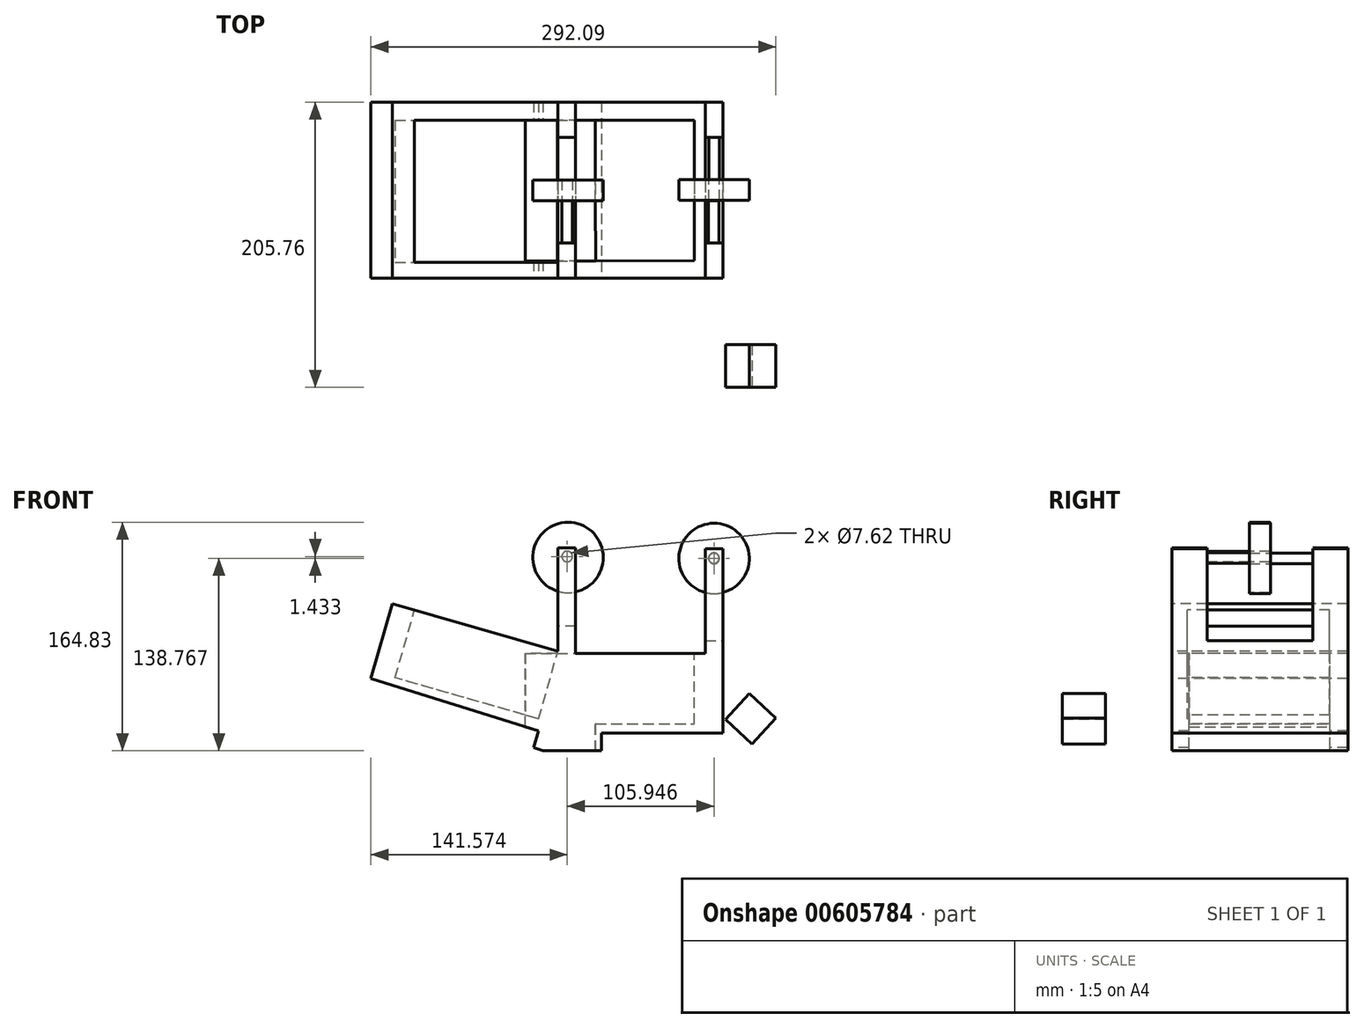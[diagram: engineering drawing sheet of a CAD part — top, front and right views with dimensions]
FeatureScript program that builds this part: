
annotation { "Feature Type Name" : "Feature", "Feature Type Description" : "" }
export const myFeature = defineFeature(function(context is Context, id is Id, definition is map)
    precondition{}
    {
        {
            var Q0;
            Q0=qCreatedBy(makeId("Front.planeOp"),FACE);
            var sketch = newSketch(context, id + "F0", { "sketchPlane" : qUnion([Q0])});
            skLineSegment(sketch, "E0", {"start": v(0, 0) * mm, "end": v(0, 57.54) * mm});
            skLineSegment(sketch, "E1", {"start": v(0, 57.54) * mm, "end": v(-113.43, 57.54) * mm});
            skLineSegment(sketch, "E2", {"start": v(-113.43, 57.54) * mm, "end": v(-238.5, 93.39) * mm});
            skLineSegment(sketch, "E3", {"start": v(-238.5, 93.39) * mm, "end": v(-254, 39.34) * mm});
            skLineSegment(sketch, "E4", {"start": v(-254, 39.34) * mm, "end": v(-127.98, 0) * mm});
            skLineSegment(sketch, "E5", {"start": v(-241.45, 83.14) * mm, "end": v(-250.88, 50.23) * mm});
            skLineSegment(sketch, "E6", {"start": v(-250.88, 50.23) * mm, "end": v(-287.5, 60.72) * mm});
            skLineSegment(sketch, "E7", {"start": v(-287.5, 60.72) * mm, "end": v(-241.45, 83.14) * mm});
            skLineSegment(sketch, "E8", {"start": v(0, 9.96) * mm, "end": v(0, 46.2) * mm});
            skLineSegment(sketch, "E9", {"start": v(0, 46.2) * mm, "end": v(38.1, 10.83) * mm});
            skLineSegment(sketch, "E10", {"start": v(38.1, 10.83) * mm, "end": v(0, 9.96) * mm});
            skLineSegment(sketch, "E11", {"start": v(-119.1, 59.16) * mm, "end": v(-119.1, 133.74) * mm});
            skLineSegment(sketch, "E12", {"start": v(-119.1, 133.74) * mm, "end": v(-106.4, 133.74) * mm});
            skLineSegment(sketch, "E13", {"start": v(-106.4, 133.74) * mm, "end": v(-106.4, 57.54) * mm});
            skLineSegment(sketch, "E14", {"start": v(-106.4, 57.54) * mm, "end": v(-113.43, 57.54) * mm});
            skLineSegment(sketch, "E15", {"start": v(0, 57.54) * mm, "end": v(0, 133.05) * mm});
            skLineSegment(sketch, "E16", {"start": v(0, 133.05) * mm, "end": v(-12.7, 133.05) * mm});
            skLineSegment(sketch, "E17", {"start": v(-12.7, 133.05) * mm, "end": v(-12.7, 57.54) * mm});
            skLineSegment(sketch, "E18", {"start": v(-12.7, 57.54) * mm, "end": v(0, 57.54) * mm});
            skLineSegment(sketch, "E19", {"start": v(-132.95, 1.55) * mm, "end": v(-136.74, -10.57) * mm});
            skLineSegment(sketch, "E20", {"start": v(-136.74, -10.57) * mm, "end": v(-129.91, -12.7) * mm});
            skLineSegment(sketch, "E21", {"start": v(-129.91, -12.7) * mm, "end": v(-87.6, -12.7) * mm});
            skLineSegment(sketch, "E22", {"start": v(-87.6, -12.7) * mm, "end": v(-87.6, 0) * mm});
            skLineSegment(sketch, "E23", {"start": v(-87.6, 0) * mm, "end": v(-127.98, 0) * mm});
            skLineSegment(sketch, "E24", {"start": v(19.05, 28.52) * mm, "end": v(43.47, 28.52) * mm});
            skLineSegment(sketch, "E25", {"start": v(43.47, 28.52) * mm, "end": v(43.47, 41.22) * mm});
            skLineSegment(sketch, "E26", {"start": v(43.47, 41.22) * mm, "end": v(5.37, 41.22) * mm});
            skLineSegment(sketch, "E27", {"start": v(5.37, 41.22) * mm, "end": v(19.05, 28.52) * mm});
            skLineSegment(sketch, "E28", {"start": v(0, 9.96) * mm, "end": v(0, 0) * mm});
            skLineSegment(sketch, "E29", {"start": v(-87.6, 0) * mm, "end": v(0, 0) * mm});
            skSolve(sketch);
        }
        {
            var Q0;
            Q0=makeQuery(id+"F0.imprint","IMPRINT",FACE,{"disambiguationData":[TD([[makeQuery(id+"F0.imprint","IMPRINT",EDGE,{"derivedFrom":sQuery(id+"F0.wireOp",EDGE,"E0")}),1.0]])]});
            var Q1;
            Q1=makeQuery(id+"F0.imprint","IMPRINT",FACE,{"disambiguationData":[TD([[makeQuery(id+"F0.imprint","IMPRINT",EDGE,{"derivedFrom":sQuery(id+"F0.wireOp",EDGE,"E5")}),-1.0]])]});
            var Q2;
            {var subQ0=sQuery(id+"F0.wireOp",EDGE,"E19");Q2=makeQuery(id+"F0.imprint","IMPRINT",FACE,{"disambiguationData":[TD([[makeQuery(id+"F0.imprint","IMPRINT",EDGE,{"derivedFrom":subQ0}),1.0]])]});}
            var Q3;
            {var subQ0=sQuery(id+"F0.wireOp",EDGE,"E11");Q3=makeQuery(id+"F0.imprint","IMPRINT",FACE,{"disambiguationData":[TD([[makeQuery(id+"F0.imprint","IMPRINT",EDGE,{"derivedFrom":subQ0}),-1.0]])]});}
            var Q4;
            Q4=makeQuery(id+"F0.imprint","IMPRINT",FACE,{"disambiguationData":[TD([[makeQuery(id+"F0.imprint","IMPRINT",EDGE,{"derivedFrom":sQuery(id+"F0.wireOp",EDGE,"E15")}),1.0]])]});
            var Q5;
            Q5=makeQuery(id+"F0.imprint","IMPRINT",FACE,{"disambiguationData":[TD([[makeQuery(id+"F0.imprint","IMPRINT",EDGE,{"derivedFrom":sQuery(id+"F0.wireOp",EDGE,"E24")}),1.0]])]});
            var Q6;
            {var subQ3=sQuery(id+"F0.wireOp",EDGE,"E8");Q6=makeQuery(id+"F0.imprint","IMPRINT",FACE,{"disambiguationData":[TD([[makeQuery(id+"F0.imprint","IMPRINT",EDGE,{"derivedFrom":subQ3}),-1.0]])]});}
            extrude(context, id + "F1", {"entities" : qUnion([Q0, Q1, Q2, Q3, Q4, Q5, Q6]), "oppositeDirection" : true, "depth" : 127 * mm, "offsetDistance" : 25.4 * mm});
        }
        {
            var Q0;
            Q0=makeQuery(id+"F1.opExtrude","SWEPT_FACE",FACE,{"disambiguationData":[OSD([sQuery(id+"F0.wireOp",EDGE,"E0"),sQuery(id+"F0.wireOp",EDGE,"E15")])]});
            var sketch = newSketch(context, id + "F2", { "sketchPlane" : qUnion([Q0])});
            skLineSegment(sketch, "E30", {"start": v(25.4, 133.05) * mm, "end": v(25.4, 66.79) * mm});
            skLineSegment(sketch, "E31", {"start": v(25.4, 66.79) * mm, "end": v(101.6, 66.79) * mm});
            skLineSegment(sketch, "E32", {"start": v(101.6, 66.79) * mm, "end": v(101.6, 133.05) * mm});
            skLineSegment(sketch, "E33", {"start": v(101.6, 133.05) * mm, "end": v(25.4, 133.05) * mm});
            skSolve(sketch);
        }
        {
            var Q0;
            Q0=makeQuery(id+"F2.imprint","IMPRINT",FACE,{"disambiguationData":[TD([[makeQuery(id+"F2.imprint","IMPRINT",EDGE,{"derivedFrom":sQuery(id+"F2.wireOp",EDGE,"E30")}),1.0]])]});
            extrude(context, id + "F3", {"entities" : qUnion([Q0]), "operationType" : NewBodyOperationType.REMOVE, "oppositeDirection" : true, "depth" : 25.4 * mm, "offsetDistance" : 25.4 * mm});
        }
        {
            var Q0;
            Q0=makeQuery(id+"F1.opExtrude","SWEPT_FACE",FACE,{"disambiguationData":[OSD([sQuery(id+"F0.wireOp",EDGE,"E11")])]});
            var sketch = newSketch(context, id + "F4", { "sketchPlane" : qUnion([Q0])});
            skLineSegment(sketch, "E34", {"start": v(-101.6, 133.74) * mm, "end": v(-101.6, 77.1) * mm});
            skLineSegment(sketch, "E35", {"start": v(-101.6, 77.1) * mm, "end": v(-25.4, 77.1) * mm});
            skLineSegment(sketch, "E36", {"start": v(-25.4, 77.1) * mm, "end": v(-25.4, 133.74) * mm});
            skLineSegment(sketch, "E37", {"start": v(-25.4, 133.74) * mm, "end": v(-101.6, 133.74) * mm});
            skSolve(sketch);
        }
        {
            var Q0;
            Q0=makeQuery(id+"F4.imprint","IMPRINT",FACE,{"disambiguationData":[TD([[makeQuery(id+"F4.imprint","IMPRINT",EDGE,{"derivedFrom":sQuery(id+"F4.wireOp",EDGE,"E34")}),1.0]])]});
            extrude(context, id + "F5", {"entities" : qUnion([Q0]), "operationType" : NewBodyOperationType.REMOVE, "oppositeDirection" : true, "depth" : 25.4 * mm, "offsetDistance" : 25.4 * mm});
        }
        {
            var Q0;
            Q0=makeQuery(id+"F1.opExtrude","SWEPT_FACE",FACE,{"disambiguationData":[OSD([sQuery(id+"F0.wireOp",EDGE,"E1")])]});
            var sketch = newSketch(context, id + "F6", { "sketchPlane" : qUnion([Q0])});
            skLineSegment(sketch, "E38", {"start": v(-91.85, 114.1) * mm, "end": v(-20.73, 114.1) * mm});
            skLineSegment(sketch, "E39", {"start": v(-20.73, 114.1) * mm, "end": v(-20.73, 12.74) * mm});
            skLineSegment(sketch, "E40", {"start": v(-91.85, 114.1) * mm, "end": v(-91.85, 12.5) * mm});
            skLineSegment(sketch, "E41", {"start": v(-91.85, 12.5) * mm, "end": v(-20.73, 12.74) * mm});
            skSolve(sketch);
        }
        {
            var Q0;
            Q0=makeQuery(id+"F6.imprint","IMPRINT",FACE,{"disambiguationData":[TD([[makeQuery(id+"F6.imprint","IMPRINT",EDGE,{"derivedFrom":sQuery(id+"F6.wireOp",EDGE,"E38")}),-1.0]])]});
            extrude(context, id + "F7", {"entities" : qUnion([Q0]), "operationType" : NewBodyOperationType.REMOVE, "oppositeDirection" : true, "depth" : 50.8 * mm, "offsetDistance" : 25.4 * mm});
        }
        {
            var Q0;
            Q0=makeQuery(id+"F1.opExtrude","SWEPT_FACE",FACE,{"disambiguationData":[OSD([sQuery(id+"F0.wireOp",EDGE,"E2")])]});
            var sketch = newSketch(context, id + "F8", { "sketchPlane" : qUnion([Q0])});
            skLineSegment(sketch, "E42.bottom", {"start": v(-238.44, 112.66) * mm, "end": v(-147, 112.66) * mm});
            skLineSegment(sketch, "E42.top", {"start": v(-238.44, 16.14) * mm, "end": v(-147, 16.14) * mm});
            skLineSegment(sketch, "E42.left", {"start": v(-238.44, 112.66) * mm, "end": v(-238.44, 16.14) * mm});
            skLineSegment(sketch, "E42.right", {"start": v(-147, 112.66) * mm, "end": v(-147, 16.14) * mm});
            skSolve(sketch);
        }
        {
            var Q0;
            Q0=makeQuery(id+"F8.imprint","IMPRINT",FACE,{"disambiguationData":[TD([[makeQuery(id+"F8.imprint","IMPRINT",EDGE,{"derivedFrom":sQuery(id+"F8.wireOp",EDGE,"E42.bottom")}),-1.0]])]});
            extrude(context, id + "F9", {"entities" : qUnion([Q0]), "operationType" : NewBodyOperationType.REMOVE, "oppositeDirection" : true, "depth" : 50.8 * mm, "offsetDistance" : 25.4 * mm});
        }
        {
            var Q0;
            Q0=makeQuery(id+"F7.boolean.opBoolean","COPY",FACE,{"derivedFrom":makeQuery(id+"F7.opExtrude","SWEPT_FACE",FACE,{"disambiguationData":[OSD([sQuery(id+"F6.wireOp",EDGE,"E40")])]})});
            extrude(context, id + "F10", {"entities" : qUnion([Q0]), "operationType" : NewBodyOperationType.REMOVE, "oppositeDirection" : true, "depth" : 50.8 * mm, "offsetDistance" : 25.4 * mm});
        }
        {
            var Q0;
            {var subQ1=sQuery(id+"F8.wireOp",EDGE,"E42.right");Q0=makeQuery(id+"F10.boolean.opBoolean","SPLIT",FACE,{"disambiguationData":[TD([makeQuery(id+"F10.opExtrude","CAP_FACE",FACE,{"disambiguationData":[OSD([sQuery(id+"F6.wireOp",EDGE,"E40")])],"isStart":false})])],"derivedFrom":makeQuery(id+"F9.boolean.opBoolean","COPY",FACE,{"derivedFrom":makeQuery(id+"F9.opExtrude","SWEPT_FACE",FACE,{"disambiguationData":[OSD([subQ1])]})})});}
            extrude(context, id + "F11", {"entities" : qUnion([Q0]), "operationType" : NewBodyOperationType.REMOVE, "oppositeDirection" : true, "depth" : 25.4 * mm, "offsetDistance" : 25.4 * mm});
        }
        {
            var Q0;
            Q0=makeQuery(id+"F1.opExtrude","SWEPT_FACE",FACE,{"disambiguationData":[OSD([sQuery(id+"F0.wireOp",EDGE,"E2")])]});
            var sketch = newSketch(context, id + "F12", { "sketchPlane" : qUnion([Q0])});
            skLineSegment(sketch, "E43", {"start": v(-147, 112.66) * mm, "end": v(-130.78, 112.66) * mm});
            skLineSegment(sketch, "E44", {"start": v(-130.78, 112.66) * mm, "end": v(-130.78, 16.14) * mm});
            skLineSegment(sketch, "E45", {"start": v(-130.78, 16.14) * mm, "end": v(-147, 16.14) * mm});
            skLineSegment(sketch, "E46", {"start": v(-147, 16.14) * mm, "end": v(-147, 112.66) * mm});
            skSolve(sketch);
        }
        {
            var Q0;
            Q0=makeQuery(id+"F12.imprint","IMPRINT",FACE,{"disambiguationData":[TD([[makeQuery(id+"F12.imprint","IMPRINT",EDGE,{"derivedFrom":sQuery(id+"F12.wireOp",EDGE,"E43")}),-1.0]])]});
            extrude(context, id + "F13", {"entities" : qUnion([Q0]), "operationType" : NewBodyOperationType.REMOVE, "oppositeDirection" : true, "depth" : 25.4 * mm, "offsetDistance" : 25.4 * mm});
        }
        {
            var Q0;
            Q0=makeQuery(id+"F1.opExtrude","SWEPT_FACE",FACE,{"disambiguationData":[OSD([sQuery(id+"F0.wireOp",EDGE,"E2")])]});
            var sketch = newSketch(context, id + "F14", { "sketchPlane" : qUnion([Q0])});
            skLineSegment(sketch, "E47", {"start": v(-130.78, 16.14) * mm, "end": v(-130.78, 11.35) * mm});
            skLineSegment(sketch, "E48", {"start": v(-130.78, 11.35) * mm, "end": v(-238.44, 11.35) * mm});
            skLineSegment(sketch, "E49", {"start": v(-238.44, 11.35) * mm, "end": v(-238.44, 16.14) * mm});
            skLineSegment(sketch, "E50", {"start": v(-238.44, 16.14) * mm, "end": v(-130.78, 16.14) * mm});
            skSolve(sketch);
        }
        {
            var Q0;
            Q0=makeQuery(id+"F14.imprint","IMPRINT",FACE,{"disambiguationData":[TD([[makeQuery(id+"F14.imprint","IMPRINT",EDGE,{"derivedFrom":sQuery(id+"F14.wireOp",EDGE,"E47")}),-1.0]])]});
            extrude(context, id + "F15", {"entities" : qUnion([Q0]), "operationType" : NewBodyOperationType.REMOVE, "oppositeDirection" : true, "depth" : 50.8 * mm, "offsetDistance" : 25.4 * mm});
        }
        {
            var Q0;
            Q0=makeQuery(id+"F1.opExtrude","SWEPT_FACE",FACE,{"disambiguationData":[OSD([sQuery(id+"F0.wireOp",EDGE,"E2")])]});
            var sketch = newSketch(context, id + "F16", { "sketchPlane" : qUnion([Q0])});
            skLineSegment(sketch, "E51", {"start": v(-130.78, 112.66) * mm, "end": v(-130.78, 113.93) * mm});
            skLineSegment(sketch, "E52", {"start": v(-130.78, 113.93) * mm, "end": v(-238.44, 113.93) * mm});
            skLineSegment(sketch, "E53", {"start": v(-238.44, 113.93) * mm, "end": v(-238.44, 112.66) * mm});
            skLineSegment(sketch, "E54", {"start": v(-238.44, 112.66) * mm, "end": v(-130.78, 112.66) * mm});
            skSolve(sketch);
        }
        {
            var Q0;
            Q0=makeQuery(id+"F16.imprint","IMPRINT",FACE,{"disambiguationData":[TD([[makeQuery(id+"F16.imprint","IMPRINT",EDGE,{"derivedFrom":sQuery(id+"F16.wireOp",EDGE,"E51")}),-1.0]])]});
            extrude(context, id + "F17", {"entities" : qUnion([Q0]), "operationType" : NewBodyOperationType.REMOVE, "oppositeDirection" : true, "depth" : 50.8 * mm, "offsetDistance" : 25.4 * mm});
        }
        {
            var Q0;
            {var subQ0=sQuery(id+"F6.wireOp",EDGE,"E40");Q0=makeQuery(id+"F10.boolean.opBoolean","MERGE",FACE,{"derivedFrom":[makeQuery(id+"F7.boolean.opBoolean","COPY",FACE,{"derivedFrom":makeQuery(id+"F7.opExtrude","CAP_FACE",FACE,{"disambiguationData":[OSD([sQuery(id+"F6.wireOp",EDGE,"E38"),sQuery(id+"F6.wireOp",EDGE,"E39"),subQ0,sQuery(id+"F6.wireOp",EDGE,"E41")])],"isStart":false})}),makeQuery(id+"F10.opExtrude","SWEPT_FACE",FACE,{"disambiguationData":[OSD([subQ0]),TDD([makeQuery(id+"F7.boolean.opBoolean","COPY",EDGE,{"derivedFrom":makeQuery(id+"F7.opExtrude","CAP_EDGE",EDGE,{"disambiguationData":[OSD([subQ0])],"isStart":false})})])]})]});}
            var sketch = newSketch(context, id + "F18", { "sketchPlane" : qUnion([Q0])});
            skLineSegment(sketch, "E55", {"start": v(-142.65, 114.1) * mm, "end": v(-142.65, 12.5) * mm});
            skLineSegment(sketch, "E56", {"start": v(-142.65, 12.5) * mm, "end": v(-117.25, 12.5) * mm});
            skLineSegment(sketch, "E57", {"start": v(-117.25, 12.5) * mm, "end": v(-117.25, 114.1) * mm});
            skLineSegment(sketch, "E58", {"start": v(-117.25, 114.1) * mm, "end": v(-142.65, 114.1) * mm});
            skSolve(sketch);
        }
        {
            var Q0;
            Q0=makeQuery(id+"F18.imprint","IMPRINT",FACE,{"disambiguationData":[TD([[makeQuery(id+"F18.imprint","IMPRINT",EDGE,{"derivedFrom":sQuery(id+"F18.wireOp",EDGE,"E55")}),1.0]])]});
            extrude(context, id + "F19", {"entities" : qUnion([Q0]), "operationType" : NewBodyOperationType.REMOVE, "oppositeDirection" : true, "depth" : 50.8 * mm, "offsetDistance" : 25.4 * mm});
        }
        {
            var Q0;
            {var subQ0=sQuery(id+"F6.wireOp",EDGE,"E40");Q0=makeQuery(id+"F10.boolean.opBoolean","MERGE",FACE,{"derivedFrom":[makeQuery(id+"F7.boolean.opBoolean","COPY",FACE,{"derivedFrom":makeQuery(id+"F7.opExtrude","CAP_FACE",FACE,{"disambiguationData":[OSD([sQuery(id+"F6.wireOp",EDGE,"E38"),sQuery(id+"F6.wireOp",EDGE,"E39"),subQ0,sQuery(id+"F6.wireOp",EDGE,"E41")])],"isStart":false})}),makeQuery(id+"F10.opExtrude","SWEPT_FACE",FACE,{"disambiguationData":[OSD([subQ0]),TDD([makeQuery(id+"F7.boolean.opBoolean","COPY",EDGE,{"derivedFrom":makeQuery(id+"F7.opExtrude","CAP_EDGE",EDGE,{"disambiguationData":[OSD([subQ0])],"isStart":false})})])]})]});}
            var sketch = newSketch(context, id + "F20", { "sketchPlane" : qUnion([Q0])});
            skLineSegment(sketch, "E59", {"start": v(-104.55, 12.5) * mm, "end": v(-91.85, 12.5) * mm});
            skLineSegment(sketch, "E60", {"start": v(-91.85, 12.5) * mm, "end": v(-92.2, 114.1) * mm});
            skLineSegment(sketch, "E61", {"start": v(-92.2, 114.1) * mm, "end": v(-130.3, 114.1) * mm});
            skLineSegment(sketch, "E62", {"start": v(-130.3, 114.1) * mm, "end": v(-130.3, 12.5) * mm});
            skLineSegment(sketch, "E63", {"start": v(-130.3, 12.5) * mm, "end": v(-104.55, 12.5) * mm});
            skSolve(sketch);
        }
        {
            var Q0;
            {var subQ6=sQuery(id+"F20.wireOp",EDGE,"E59");Q0=makeQuery(id+"F20.imprint","IMPRINT",FACE,{"disambiguationData":[TD([[makeQuery(id+"F20.imprint","IMPRINT",EDGE,{"derivedFrom":subQ6}),1.0]])]});}
            extrude(context, id + "F21", {"entities" : qUnion([Q0]), "operationType" : NewBodyOperationType.REMOVE, "oppositeDirection" : true, "depth" : 50.8 * mm, "offsetDistance" : 25.4 * mm});
        }
        {
            var Q0;
            {var subQ0=sQuery(id+"F0.wireOp",EDGE,"E9");Q0=makeQuery(id+"F1.opExtrude","SWEPT_FACE",FACE,{"disambiguationData":[OSD([subQ0]),TDD([makeQuery(id+"F0.imprint","IMPRINT",EDGE,{"disambiguationData":[TD([[makeQuery(id+"F0.imprint","INTERSECT",VERTEX,{"derivedFrom":[subQ0,sQuery(id+"F0.wireOp",EDGE,"E10")]}),1.0]])],"derivedFrom":subQ0})])]});}
            var sketch = newSketch(context, id + "F22", { "sketchPlane" : qUnion([Q0])});
            skLineSegment(sketch, "E64.bottom", {"start": v(-5.45, 47.97) * mm, "end": v(20.54, 47.97) * mm});
            skLineSegment(sketch, "E64.top", {"start": v(-5.45, 78.76) * mm, "end": v(20.54, 78.76) * mm});
            skLineSegment(sketch, "E64.left", {"start": v(-5.45, 47.97) * mm, "end": v(-5.45, 78.76) * mm});
            skLineSegment(sketch, "E64.right", {"start": v(20.54, 47.97) * mm, "end": v(20.54, 78.76) * mm});
            skSolve(sketch);
        }
        {
            var Q0;
            Q0=makeQuery(id+"F22.imprint","IMPRINT",FACE,{"disambiguationData":[TD([[makeQuery(id+"F22.imprint","IMPRINT",EDGE,{"derivedFrom":sQuery(id+"F22.wireOp",EDGE,"E64.bottom")}),1.0]])]});
            extrude(context, id + "F23", {"entities" : qUnion([Q0]), "operationType" : NewBodyOperationType.ADD, "depth" : 50.8 * mm, "offsetDistance" : 25.4 * mm});
        }
        {
            var Q0;
            {var subQ1=sQuery(id+"F0.wireOp",EDGE,"E25");Q0=makeQuery(id+"F23.boolean.opBoolean","SPLIT",FACE,{"disambiguationData":[TD([makeQuery(id+"F23.opExtrude","SWEPT_FACE",FACE,{"disambiguationData":[OSD([sQuery(id+"F22.wireOp",EDGE,"E64.bottom")])]})])],"derivedFrom":makeQuery(id+"F1.opExtrude","SWEPT_FACE",FACE,{"disambiguationData":[OSD([subQ1])]})});}
            var Q1;
            {var subQ1=sQuery(id+"F0.wireOp",EDGE,"E25");Q1=makeQuery(id+"F23.boolean.opBoolean","SPLIT",FACE,{"disambiguationData":[TD([makeQuery(id+"F23.opExtrude","SWEPT_FACE",FACE,{"disambiguationData":[OSD([sQuery(id+"F22.wireOp",EDGE,"E64.top")])]})])],"derivedFrom":makeQuery(id+"F1.opExtrude","SWEPT_FACE",FACE,{"disambiguationData":[OSD([subQ1])]})});}
            extrude(context, id + "F24", {"entities" : qUnion([Q0, Q1]), "operationType" : NewBodyOperationType.REMOVE, "oppositeDirection" : true, "depth" : 43.18 * mm, "offsetDistance" : 25.4 * mm});
        }
        {
            var Q0;
            Q0=makeQuery(id+"F23.opExtrude","CAP_FACE",FACE,{"disambiguationData":[OSD([sQuery(id+"F22.wireOp",EDGE,"E64.bottom"),sQuery(id+"F22.wireOp",EDGE,"E64.top"),sQuery(id+"F22.wireOp",EDGE,"E64.left"),sQuery(id+"F22.wireOp",EDGE,"E64.right")])],"isStart":false});
            extrude(context, id + "F25", {"entities" : qUnion([Q0]), "operationType" : NewBodyOperationType.REMOVE, "oppositeDirection" : true, "depth" : 25.4 * mm, "offsetDistance" : 25.4 * mm});
        }
        {
            var Q0;
            Q0=makeQuery(id+"F3.boolean.opBoolean","COPY",FACE,{"derivedFrom":makeQuery(id+"F3.opExtrude","SWEPT_FACE",FACE,{"disambiguationData":[OSD([sQuery(id+"F2.wireOp",EDGE,"E32")])]})});
            var sketch = newSketch(context, id + "F26", { "sketchPlane" : qUnion([Q0])});
            skCircle(sketch, "E65", {"center": v(-6.48, 126.07) * mm, "radius": 3.81 * mm});
            skSolve(sketch);
        }
        {
            var Q0;
            Q0=makeQuery(id+"F26.imprint","IMPRINT",FACE,{"disambiguationData":[TD([[makeQuery(id+"F26.imprint","IMPRINT",EDGE,{"derivedFrom":sQuery(id+"F26.wireOp",EDGE,"E65")}),1.0]])]});
            extrude(context, id + "F27", {"entities" : qUnion([Q0]), "operationType" : NewBodyOperationType.ADD, "depth" : 30.48 * mm, "offsetDistance" : 25.4 * mm});
        }
        {
            var Q0;
            Q0=makeQuery(id+"F3.boolean.opBoolean","COPY",FACE,{"derivedFrom":makeQuery(id+"F3.opExtrude","SWEPT_FACE",FACE,{"disambiguationData":[OSD([sQuery(id+"F2.wireOp",EDGE,"E30")])]})});
            var sketch = newSketch(context, id + "F28", { "sketchPlane" : qUnion([Q0])});
            skCircle(sketch, "E66", {"center": v(6.65, 126.29) * mm, "radius": 3.81 * mm});
            skSolve(sketch);
        }
        {
            var Q0;
            Q0=makeQuery(id+"F28.imprint","IMPRINT",FACE,{"disambiguationData":[TD([[makeQuery(id+"F28.imprint","IMPRINT",EDGE,{"derivedFrom":sQuery(id+"F28.wireOp",EDGE,"E66")}),1.0]])]});
            extrude(context, id + "F29", {"entities" : qUnion([Q0]), "operationType" : NewBodyOperationType.ADD, "depth" : 30.48 * mm, "offsetDistance" : 25.4 * mm});
        }
        {
            var Q0;
            Q0=makeQuery(id+"F27.opExtrude","CAP_FACE",FACE,{"disambiguationData":[OSD([sQuery(id+"F26.wireOp",EDGE,"E65")])],"isStart":false});
            var sketch = newSketch(context, id + "F30", { "sketchPlane" : qUnion([Q0])});
            skCircle(sketch, "E67", {"center": v(-6.48, 126.07) * mm, "radius": 25.4 * mm});
            skSolve(sketch);
        }
        {
            var Q0;
            Q0=makeQuery(id+"F30.imprint","IMPRINT",FACE,{"disambiguationData":[TD([[makeQuery(id+"F30.imprint","IMPRINT",EDGE,{"derivedFrom":sQuery(id+"F30.wireOp",EDGE,"E67")}),1.0]])]});
            extrude(context, id + "F31", {"entities" : qUnion([Q0]), "depth" : 15 * mm, "offsetDistance" : 25.4 * mm});
        }
        {
            var Q0;
            Q0=makeQuery(id+"F5.boolean.opBoolean","COPY",FACE,{"derivedFrom":makeQuery(id+"F5.opExtrude","SWEPT_FACE",FACE,{"disambiguationData":[OSD([sQuery(id+"F4.wireOp",EDGE,"E34")])]})});
            var sketch = newSketch(context, id + "F32", { "sketchPlane" : qUnion([Q0])});
            skCircle(sketch, "E68", {"center": v(-112.47, 126.94) * mm, "radius": 3.81 * mm});
            skSolve(sketch);
        }
        {
            var Q0;
            Q0=sQuery(id+"F32.wireOp",EDGE,"E68");
            extrude(context, id + "F33", {"bodyType" : ToolBodyType.SURFACE, "surfaceEntities" : qUnion([Q0]), "depth" : 30.48 * mm, "offsetDistance" : 25.4 * mm});
        }
        {
            var Q0;
            Q0=makeQuery(id+"F5.boolean.opBoolean","COPY",FACE,{"derivedFrom":makeQuery(id+"F5.opExtrude","SWEPT_FACE",FACE,{"disambiguationData":[OSD([sQuery(id+"F4.wireOp",EDGE,"E36")])]})});
            var sketch = newSketch(context, id + "F34", { "sketchPlane" : qUnion([Q0])});
            skCircle(sketch, "E69", {"center": v(112.43, 127.5) * mm, "radius": 3.81 * mm});
            skSolve(sketch);
        }
        {
            var Q0;
            Q0=makeQuery(id+"F34.imprint","IMPRINT",FACE,{"disambiguationData":[TD([[makeQuery(id+"F34.imprint","IMPRINT",EDGE,{"derivedFrom":sQuery(id+"F34.wireOp",EDGE,"E69")}),1.0]])]});
            extrude(context, id + "F35", {"entities" : qUnion([Q0]), "operationType" : NewBodyOperationType.ADD, "depth" : 30.48 * mm, "offsetDistance" : 25.4 * mm});
        }
        {
            var Q0;
            Q0=makeQuery(id+"F35.opExtrude","CAP_FACE",FACE,{"disambiguationData":[OSD([sQuery(id+"F34.wireOp",EDGE,"E69")])],"isStart":false});
            var sketch = newSketch(context, id + "F36", { "sketchPlane" : qUnion([Q0])});
            skCircle(sketch, "E70", {"center": v(111.8, 126.73) * mm, "radius": 25.4 * mm});
            skSolve(sketch);
        }
        {
            var Q0;
            Q0=makeQuery(id+"F36.imprint","IMPRINT",FACE,{"disambiguationData":[TD([[makeQuery(id+"F36.imprint","IMPRINT",EDGE,{"derivedFrom":sQuery(id+"F36.wireOp",EDGE,"E70")}),1.0]])]});
            extrude(context, id + "F37", {"entities" : qUnion([Q0]), "depth" : 15 * mm, "offsetDistance" : 25.4 * mm});
        }
    });
